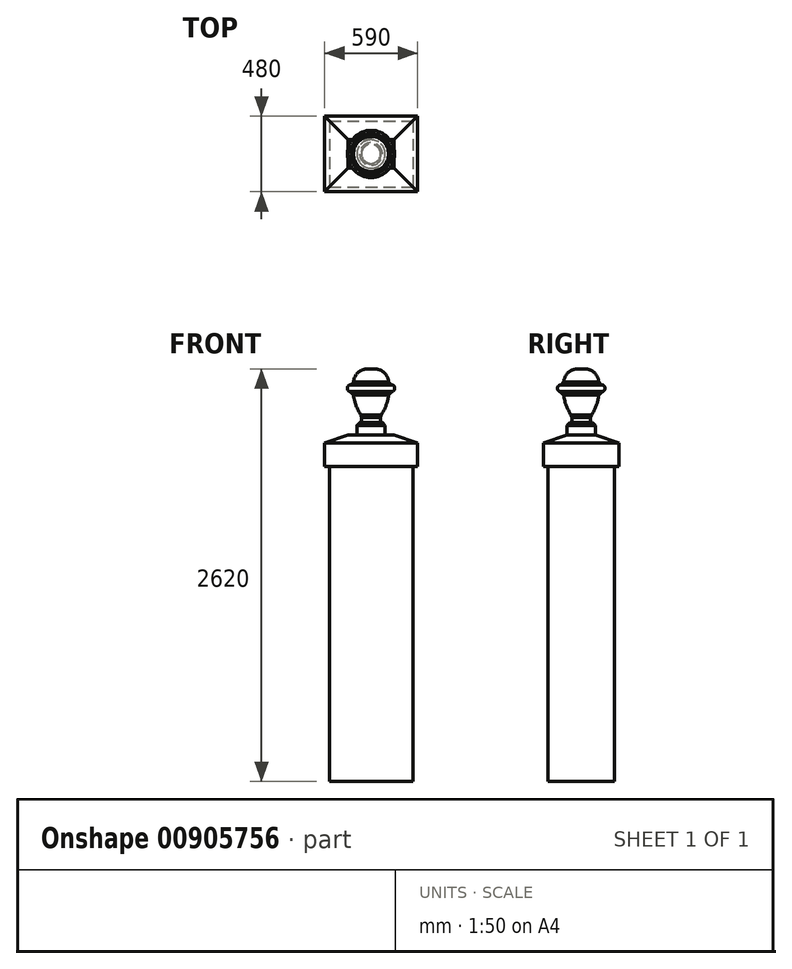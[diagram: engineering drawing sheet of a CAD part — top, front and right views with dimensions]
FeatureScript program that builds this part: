
annotation { "Feature Type Name" : "Feature", "Feature Type Description" : "" }
export const myFeature = defineFeature(function(context is Context, id is Id, definition is map)
    precondition{}
    {
        {
            var Q0;
            Q0=qCreatedBy(makeId("Top.planeOp"),FACE);
            var sketch = newSketch(context, id + "F0", { "sketchPlane" : qUnion([Q0])});
            skLineSegment(sketch, "E0.bottom", {"start": v(-265, 210) * mm, "end": v(265, 210) * mm});
            skLineSegment(sketch, "E0.top", {"start": v(-265, -210) * mm, "end": v(265, -210) * mm});
            skLineSegment(sketch, "E0.left", {"start": v(-265, 210) * mm, "end": v(-265, -210) * mm});
            skLineSegment(sketch, "E0.right", {"start": v(265, 210) * mm, "end": v(265, -210) * mm});
            skSolve(sketch);
        }
        {
            var Q0;
            Q0=qSketchRegion(id+"F0",true);
            extrude(context, id + "F1", {"entities" : qUnion([Q0]), "depth" : 2000 * mm, "offsetDistance" : 25.4 * mm});
        }
        {
            var Q0;
            Q0=makeQuery(id+"F1.opExtrude","CAP_FACE",FACE,{"disambiguationData":[OSD([sQuery(id+"F0.wireOp",EDGE,"E0.bottom"),sQuery(id+"F0.wireOp",EDGE,"E0.top"),sQuery(id+"F0.wireOp",EDGE,"E0.left"),sQuery(id+"F0.wireOp",EDGE,"E0.right")])],"isStart":false});
            var sketch = newSketch(context, id + "F2", { "sketchPlane" : qUnion([Q0])});
            skLineSegment(sketch, "E1.bottom", {"start": v(-295, 240) * mm, "end": v(295, 240) * mm});
            skLineSegment(sketch, "E1.top", {"start": v(-295, -240) * mm, "end": v(295, -240) * mm});
            skLineSegment(sketch, "E1.left", {"start": v(-295, 240) * mm, "end": v(-295, -240) * mm});
            skLineSegment(sketch, "E1.right", {"start": v(295, 240) * mm, "end": v(295, -240) * mm});
            skSolve(sketch);
        }
        {
            var Q0;
            Q0=qSketchRegion(id+"F2",true);
            extrude(context, id + "F3", {"entities" : qUnion([Q0]), "operationType" : NewBodyOperationType.ADD, "depth" : 100 * mm, "offsetDistance" : 25.4 * mm});
        }
        {
            var Q0;
            Q0=qCreatedBy(makeId("Right.planeOp"),FACE);
            var sketch = newSketch(context, id + "F4", { "sketchPlane" : qUnion([Q0])});
            skLineSegment(sketch, "E2.0", {"start": v(-240, 2100) * mm, "end": v(-240, 2000) * mm, "construction": true});
            skLineSegment(sketch, "E3.0", {"start": v(240, 2100) * mm, "end": v(-240, 2100) * mm, "construction": true});
            skLineSegment(sketch, "E4", {"start": v(-240, 2100) * mm, "end": v(-240, 2150) * mm});
            skLineSegment(sketch, "E5", {"start": v(-240, 2100) * mm, "end": v(-90, 2100) * mm});
            skLineSegment(sketch, "E6", {"start": v(-90, 2100) * mm, "end": v(-90, 2200) * mm});
            skLineSegment(sketch, "E7", {"start": v(-240, 2150) * mm, "end": v(-180.92, 2150) * mm, "construction": true});
            skLineSegment(sketch, "E8", {"start": v(-90, 2200) * mm, "end": v(-130, 2200) * mm, "construction": true});
            skLineSegment(sketch, "E9", {"start": v(-130, 2200) * mm, "end": v(-137.28, 2180) * mm, "construction": true});
            skLineSegment(sketch, "E10", {"start": v(-137.28, 2180) * mm, "end": v(-170, 2180) * mm, "construction": true});
            skLineSegment(sketch, "E11", {"start": v(-170, 2180) * mm, "end": v(-180.92, 2150) * mm, "construction": true});
            skLineSegment(sketch, "E12", {"start": v(-240, 2150) * mm, "end": v(-90, 2200) * mm});
            skSolve(sketch);
        }
        {
            var Q0;
            Q0=qSketchRegion(id+"F4",true);
            var Q1;
            Q1=makeQuery(id+"F3.opExtrude","CAP_EDGE",EDGE,{"disambiguationData":[OSD([sQuery(id+"F2.wireOp",EDGE,"E1.top")])],"isStart":false});
            var Q2;
            Q2=makeQuery(id+"F3.opExtrude","CAP_EDGE",EDGE,{"disambiguationData":[OSD([sQuery(id+"F2.wireOp",EDGE,"E1.right")])],"isStart":false});
            var Q3;
            Q3=makeQuery(id+"F3.opExtrude","CAP_EDGE",EDGE,{"disambiguationData":[OSD([sQuery(id+"F2.wireOp",EDGE,"E1.bottom")])],"isStart":false});
            var Q4;
            Q4=makeQuery(id+"F3.opExtrude","CAP_EDGE",EDGE,{"disambiguationData":[OSD([sQuery(id+"F2.wireOp",EDGE,"E1.left")])],"isStart":false});
            sweep(context, id + "F5", {"profiles" : qUnion([Q0]), "path" : qUnion([Q1, Q2, Q3, Q4])});
        }
        {
            var Q0;
            Q0=makeQuery(id+"F5.opSweep","SWEPT_FACE",FACE,{"disambiguationData":[OSD([sQuery(id+"F2.wireOp",EDGE,"E1.right"),sQuery(id+"F4.wireOp",EDGE,"E6")])]});
            var sketch = newSketch(context, id + "F6", { "sketchPlane" : qUnion([Q0])});
            skLineSegment(sketch, "E13.0", {"start": v(90, 2200) * mm, "end": v(90, 2100) * mm});
            skLineSegment(sketch, "E13.1", {"start": v(90, 2200) * mm, "end": v(-90, 2200) * mm});
            skLineSegment(sketch, "E13.2", {"start": v(90, 2100) * mm, "end": v(-90, 2100) * mm});
            skLineSegment(sketch, "E13.3", {"start": v(-90, 2200) * mm, "end": v(-90, 2100) * mm});
            skSolve(sketch);
        }
        {
            var Q0;
            Q0=qSketchRegion(id+"F6",true);
            var Q1;
            Q1=makeQuery(id+"F5.opSweep","SWEPT_FACE",FACE,{"disambiguationData":[OSD([sQuery(id+"F2.wireOp",EDGE,"E1.left"),sQuery(id+"F4.wireOp",EDGE,"E6")])]});
            var Q2;
            Q2=makeQuery(id+"F5.opSweep","MID_CAP_VERTEX",VERTEX,{"disambiguationData":[OSD([sQuery(id+"F2.wireOp",EDGE,"E1.bottom"),sQuery(id+"F4.wireOp",EDGE,"E5"),sQuery(id+"F4.wireOp",EDGE,"E6")])],"capPos":2.0});
            extrude(context, id + "F7", {"entities" : qUnion([Q0]), "operationType" : NewBodyOperationType.ADD, "endBound" : BoundingType.UP_TO_SURFACE, "depth" : 25.4 * mm, "endBoundEntityFace" : qUnion([Q1]), "endBoundEntityVertex" : qUnion([Q2]), "offsetDistance" : 25.4 * mm});
        }
        {
            var Q0;
            Q0=qCreatedBy(makeId("Right.planeOp"),FACE);
            var sketch = newSketch(context, id + "F8", { "sketchPlane" : qUnion([Q0])});
            skLineSegment(sketch, "E14", {"start": v(0, 0) * mm, "end": v(0, 2620) * mm, "construction": true});
            skLineSegment(sketch, "E15", {"start": v(0, 2620) * mm, "end": v(0, 2200) * mm});
            skLineSegment(sketch, "E16", {"start": v(0, 2620) * mm, "end": v(100, 2620) * mm});
            skLineSegment(sketch, "E17", {"start": v(100, 2620) * mm, "end": v(113.64, 2520) * mm});
            skLineSegment(sketch, "E18", {"start": v(113.64, 2520) * mm, "end": v(150, 2516.82) * mm});
            skLineSegment(sketch, "E19", {"start": v(150, 2516.82) * mm, "end": v(150, 2476.82) * mm});
            skLineSegment(sketch, "E20", {"start": v(150, 2476.82) * mm, "end": v(113.64, 2473.64) * mm});
            skArc(sketch, "E21", {"start": v(60, 2320) * mm, "mid": v(97.26, 2393.17) * mm, "end": v(113.64, 2473.64) * mm});
            skLineSegment(sketch, "E22", {"start": v(60, 2320) * mm, "end": v(60, 2280) * mm});
            skLineSegment(sketch, "E23", {"start": v(60, 2280) * mm, "end": v(90, 2280) * mm});
            skLineSegment(sketch, "E24", {"start": v(90, 2280) * mm, "end": v(90, 2200) * mm});
            skLineSegment(sketch, "E25", {"start": v(90, 2200) * mm, "end": v(0, 2200) * mm});
            skSolve(sketch);
        }
        {
            var Q0;
            Q0=qSketchRegion(id+"F8",true);
            var Q1;
            Q1=sQuery(id+"F8.wireOp",EDGE,"E14");
            revolve(context, id + "F9", {"operationType" : NewBodyOperationType.ADD, "surfaceOperationType" : NewSurfaceOperationType.NEW, "entities" : qUnion([Q0]), "axis" : qUnion([Q1]), "revolveType" : RevolveType.FULL});
        }
        {
            var Q0;
            Q0=makeQuery(id+"F9.opRevolve","SWEPT_EDGE",EDGE,{"disambiguationData":[OSD([sQuery(id+"F8.wireOp",EDGE,"E16"),sQuery(id+"F8.wireOp",EDGE,"E17")])]});
            fillet(context, id + "F10", {"entities" : qUnion([Q0]), "radius" : 88.9 * mm, "tangentPropagation" : true, "allowEdgeOverflow" : false});
        }
        {
            var Q0;
            Q0=makeQuery(id+"F9.opRevolve","SWEPT_EDGE",EDGE,{"disambiguationData":[OSD([sQuery(id+"F8.wireOp",EDGE,"E18"),sQuery(id+"F8.wireOp",EDGE,"E19")])]});
            var Q1;
            Q1=makeQuery(id+"F9.opRevolve","SWEPT_EDGE",EDGE,{"disambiguationData":[OSD([sQuery(id+"F8.wireOp",EDGE,"E19"),sQuery(id+"F8.wireOp",EDGE,"E20")])]});
            fillet(context, id + "F11", {"entities" : qUnion([Q0, Q1]), "radius" : 19.05 * mm, "tangentPropagation" : true, "allowEdgeOverflow" : false});
        }
        {
            var Q0;
            Q0=makeQuery(id+"F9.opRevolve","SWEPT_EDGE",EDGE,{"disambiguationData":[OSD([sQuery(id+"F8.wireOp",EDGE,"E20"),sQuery(id+"F8.wireOp",EDGE,"E21")])]});
            var Q1;
            Q1=makeQuery(id+"F9.opRevolve","SWEPT_EDGE",EDGE,{"disambiguationData":[OSD([sQuery(id+"F8.wireOp",EDGE,"E21"),sQuery(id+"F8.wireOp",EDGE,"E22")])]});
            chamfer(context, id + "F12", {"entities" : qUnion([Q0, Q1]), "width" : 25.4 * mm, "tangentPropagation" : true});
        }
        {
            var Q0;
            Q0=makeQuery(id+"F9.opRevolve","SWEPT_EDGE",EDGE,{"disambiguationData":[OSD([sQuery(id+"F8.wireOp",EDGE,"E22"),sQuery(id+"F8.wireOp",EDGE,"E23")])]});
            fillet(context, id + "F13", {"entities" : qUnion([Q0]), "radius" : 12.7 * mm, "tangentPropagation" : true, "allowEdgeOverflow" : false});
        }
        {
            var Q0;
            Q0=makeQuery(id+"F9.opRevolve","SWEPT_EDGE",EDGE,{"disambiguationData":[OSD([sQuery(id+"F8.wireOp",EDGE,"E23"),sQuery(id+"F8.wireOp",EDGE,"E24")])]});
            var Q1;
            Q1=makeQuery(id+"F9.opRevolve","SWEPT_EDGE",EDGE,{"disambiguationData":[OSD([sQuery(id+"F8.wireOp",EDGE,"E17"),sQuery(id+"F8.wireOp",EDGE,"E18")])]});
            chamfer(context, id + "F14", {"entities" : qUnion([Q0, Q1]), "width" : 19.05 * mm, "tangentPropagation" : true});
        }
    });
